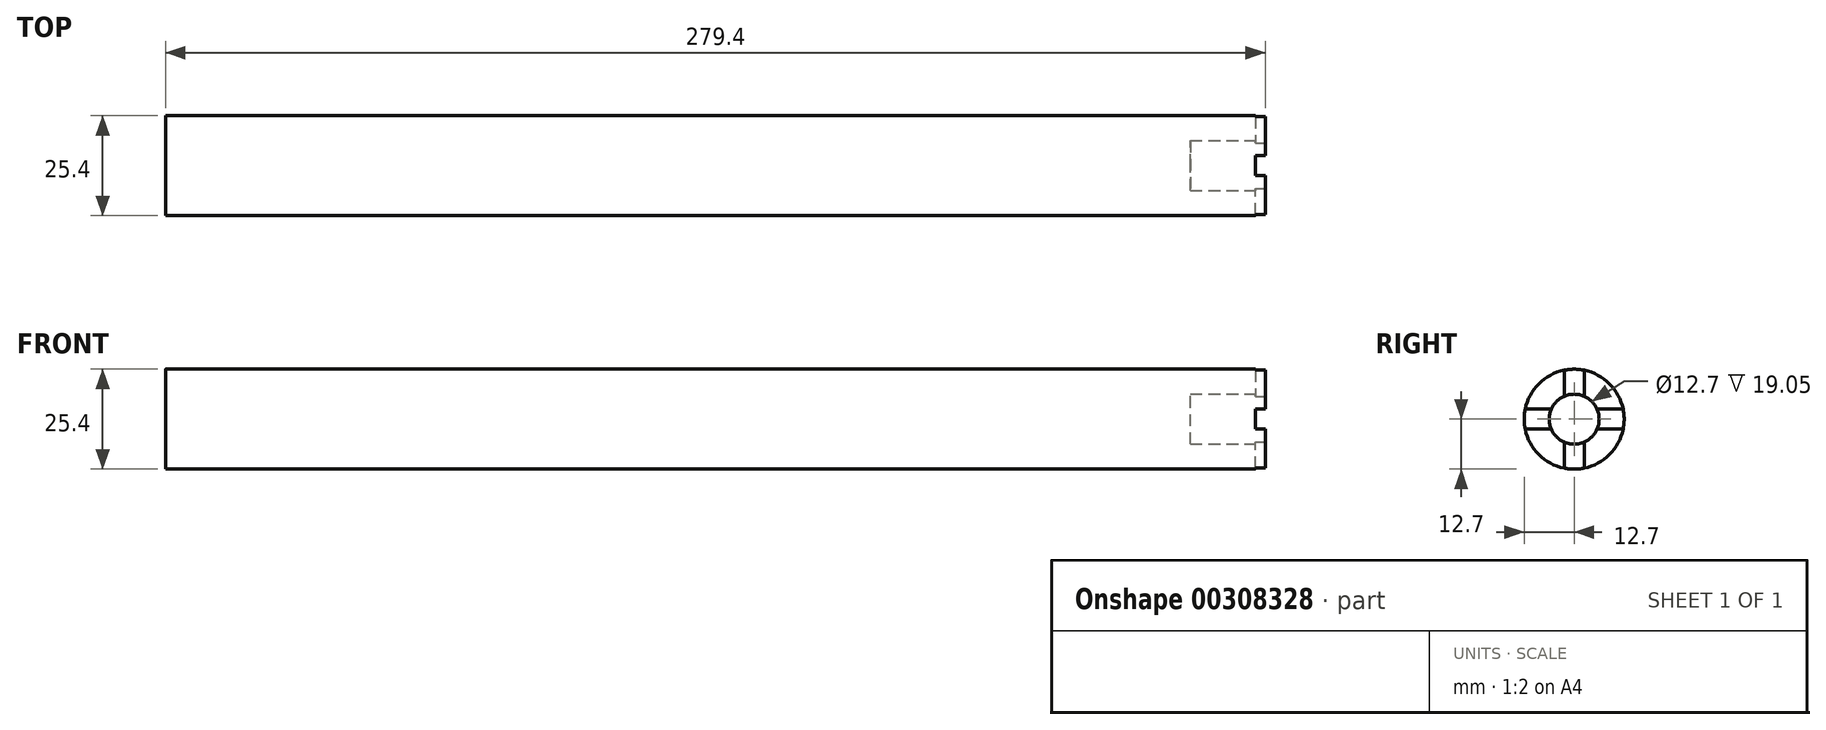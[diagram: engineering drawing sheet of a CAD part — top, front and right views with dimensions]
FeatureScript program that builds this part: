
annotation { "Feature Type Name" : "Feature", "Feature Type Description" : "" }
export const myFeature = defineFeature(function(context is Context, id is Id, definition is map)
    precondition{}
    {
        {
            var Q0;
            Q0=qCreatedBy(makeId("Right.planeOp"),FACE);
            var sketch = newSketch(context, id + "F0", { "sketchPlane" : qUnion([Q0])});
            skCircle(sketch, "E0", {"center": v(0, 0) * mm, "radius": 12.7 * mm});
            skSolve(sketch);
        }
        {
            var Q0;
            Q0 = qSketchRegion(id + "F0", true);
            extrude(context, id + "F1", {"entities" : qUnion([Q0]), "depth" : 279.4 * mm});
        }
        {
            var Q0;
            Q0=makeQuery(id+"F1.opExtrude","CAP_FACE",FACE,{"disambiguationData":[OSD([sQuery(id+"F0.wireOp",EDGE,"E0")])],"isStart":false});
            var sketch = newSketch(context, id + "F2", { "sketchPlane" : qUnion([Q0])});
            skCircle(sketch, "E1", {"center": v(0, 0) * mm, "radius": 6.35 * mm});
            skSolve(sketch);
        }
        {
            var Q0;
            Q0 = qSketchRegion(id + "F2", true);
            extrude(context, id + "F3", {"entities" : qUnion([Q0]), "operationType" : NewBodyOperationType.REMOVE, "oppositeDirection" : true, "depth" : 19.05 * mm});
        }
        {
            var Q0;
            Q0=makeQuery(id+"F1.opExtrude","CAP_FACE",FACE,{"disambiguationData":[OSD([sQuery(id+"F0.wireOp",EDGE,"E0")])],"isStart":false});
            var sketch = newSketch(context, id + "F4", { "sketchPlane" : qUnion([Q0])});
            skLineSegment(sketch, "E2", {"start": v(0, 16.46) * mm, "end": v(0, -25.05) * mm, "construction": true});
            skLineSegment(sketch, "E3", {"start": v(-26.37, 0) * mm, "end": v(25.47, 0) * mm, "construction": true});
            skLineSegment(sketch, "E4.MirrorCS", {"start": v(26.37, 0) * mm, "end": v(-25.47, 0) * mm, "construction": true});
            skLineSegment(sketch, "E5", {"start": v(-12.44, -2.54) * mm, "end": v(-5.82, -2.54) * mm});
            skLineSegment(sketch, "E6.MirrorCS", {"start": v(-12.44, 2.54) * mm, "end": v(-5.82, 2.54) * mm});
            skLineSegment(sketch, "E7.MirrorCS", {"start": v(12.44, 2.54) * mm, "end": v(5.82, 2.54) * mm});
            skLineSegment(sketch, "E8.MirrorCS", {"start": v(12.44, -2.54) * mm, "end": v(5.82, -2.54) * mm});
            skLineSegment(sketch, "E9", {"start": v(-2.54, 12.44) * mm, "end": v(-2.54, 5.82) * mm});
            skLineSegment(sketch, "E10.MirrorCS", {"start": v(2.54, 12.44) * mm, "end": v(2.54, 5.82) * mm});
            skLineSegment(sketch, "E11.MirrorCS", {"start": v(-2.54, -12.44) * mm, "end": v(-2.54, -5.82) * mm});
            skLineSegment(sketch, "E12.MirrorCS", {"start": v(2.54, -12.44) * mm, "end": v(2.54, -5.82) * mm});
            skSolve(sketch);
        }
        {
            var Q0;
            {var subQ0=sQuery(id+"F4.wireOp",EDGE,"E9");Q0=makeQuery(id+"F4.imprint","IMPRINT",FACE,{"disambiguationData":[TD([[makeQuery(id+"F4.imprint","IMPRINT",EDGE,{"derivedFrom":subQ0}),1.0]])]});}
            var Q1;
            {var subQ0=sQuery(id+"F4.wireOp",EDGE,"E5");Q1=makeQuery(id+"F4.imprint","IMPRINT",FACE,{"disambiguationData":[TD([[makeQuery(id+"F4.imprint","IMPRINT",EDGE,{"derivedFrom":subQ0}),1.0]])]});}
            var Q2;
            {var subQ0=sQuery(id+"F4.wireOp",EDGE,"E7.MirrorCS");Q2=makeQuery(id+"F4.imprint","IMPRINT",FACE,{"disambiguationData":[TD([[makeQuery(id+"F4.imprint","IMPRINT",EDGE,{"derivedFrom":subQ0}),1.0]])]});}
            var Q3;
            {var subQ0=sQuery(id+"F4.wireOp",EDGE,"E11.MirrorCS");Q3=makeQuery(id+"F4.imprint","IMPRINT",FACE,{"disambiguationData":[TD([[makeQuery(id+"F4.imprint","IMPRINT",EDGE,{"derivedFrom":subQ0}),-1.0]])]});}
            extrude(context, id + "F5", {"entities" : qUnion([Q0, Q1, Q2, Q3]), "operationType" : NewBodyOperationType.REMOVE, "oppositeDirection" : true, "depth" : 2.54 * mm});
        }
    });
